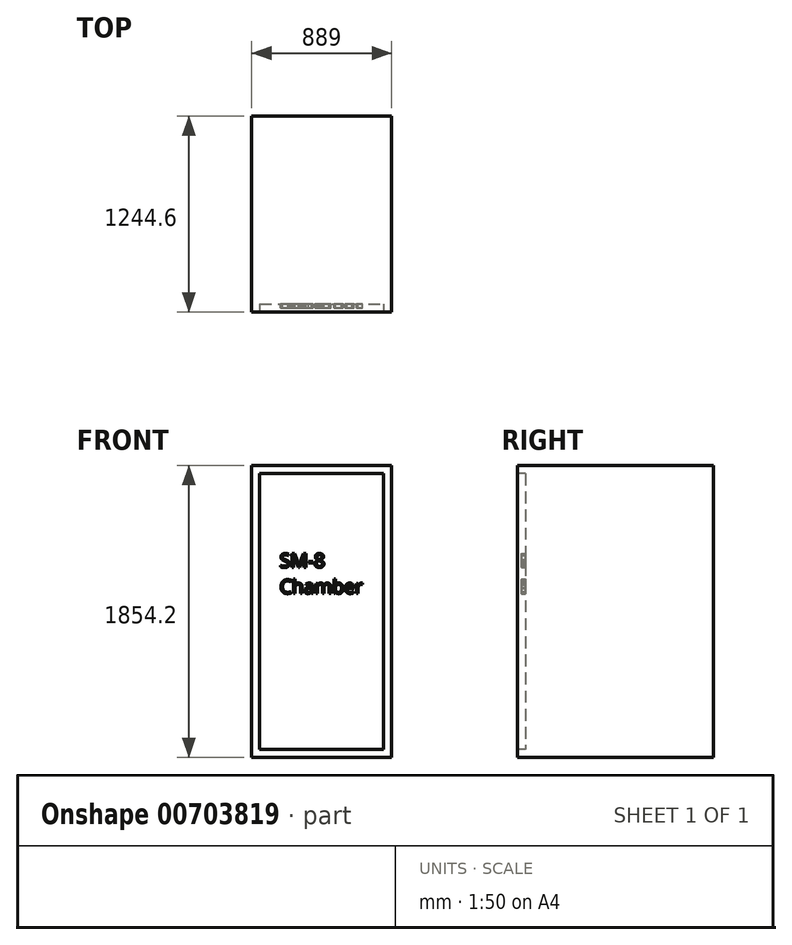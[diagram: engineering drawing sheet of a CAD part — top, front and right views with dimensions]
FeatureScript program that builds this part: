
annotation { "Feature Type Name" : "Feature", "Feature Type Description" : "" }
export const myFeature = defineFeature(function(context is Context, id is Id, definition is map)
    precondition{}
    {
        {
            var Q0;
            Q0=qCreatedBy(makeId("Top.planeOp"),FACE);
            var sketch = newSketch(context, id + "F0", { "sketchPlane" : qUnion([Q0])});
            skLineSegment(sketch, "E0.bottom", {"start": v(444.5, -622.3) * mm, "end": v(-444.5, -622.3) * mm});
            skLineSegment(sketch, "E0.top", {"start": v(444.5, 622.3) * mm, "end": v(-444.5, 622.3) * mm});
            skLineSegment(sketch, "E0.left", {"start": v(444.5, -622.3) * mm, "end": v(444.5, 622.3) * mm});
            skLineSegment(sketch, "E0.right", {"start": v(-444.5, -622.3) * mm, "end": v(-444.5, 622.3) * mm});
            skPoint(sketch, "E0.middle", {"position": v(0, 0) * mm});
            skSolve(sketch);
        }
        {
            var Q0;
            Q0 = qSketchRegion(id + "F0", true);
            extrude(context, id + "F1", {"entities" : qUnion([Q0]), "depth" : 1854.2 * mm, "offsetDistance" : 25.4 * mm});
        }
        {
            var Q0;
            Q0=makeQuery(id+"F1.opExtrude","SWEPT_FACE",FACE,{"disambiguationData":[OSD([sQuery(id+"F0.wireOp",EDGE,"E0.bottom")])]});
            var sketch = newSketch(context, id + "F2", { "sketchPlane" : qUnion([Q0])});
            skLineSegment(sketch, "E1.bottom", {"start": v(-393.7, 1803.4) * mm, "end": v(393.7, 1803.4) * mm});
            skLineSegment(sketch, "E1.top", {"start": v(-393.7, 50.8) * mm, "end": v(393.7, 50.8) * mm});
            skLineSegment(sketch, "E1.left", {"start": v(-393.7, 1803.4) * mm, "end": v(-393.7, 50.8) * mm});
            skLineSegment(sketch, "E1.right", {"start": v(393.7, 1803.4) * mm, "end": v(393.7, 50.8) * mm});
            skSolve(sketch);
        }
        {
            var Q0;
            Q0 = qSketchRegion(id + "F2", true);
            extrude(context, id + "F3", {"entities" : qUnion([Q0]), "operationType" : NewBodyOperationType.REMOVE, "oppositeDirection" : true, "depth" : 50.8 * mm, "offsetDistance" : 25.4 * mm});
        }
        {
            var Q0;
            Q0=makeQuery(id+"F3.boolean.opBoolean","COPY",FACE,{"derivedFrom":makeQuery(id+"F3.opExtrude","CAP_FACE",FACE,{"disambiguationData":[OSD([sQuery(id+"F2.wireOp",EDGE,"E1.bottom"),sQuery(id+"F2.wireOp",EDGE,"E1.top"),sQuery(id+"F2.wireOp",EDGE,"E1.left"),sQuery(id+"F2.wireOp",EDGE,"E1.right")])],"isStart":false})});
            var sketch = newSketch(context, id + "F4", { "sketchPlane" : qUnion([Q0])});
            skText(sketch, "E2", { "text": "SM-8\nChamber\n", "fontName": "OpenSans-Regular.ttf"});
            const initialGuessF4  = {"E2": [-0.2667, 1.2074, 1, 0, 0.088]};
            skSetInitialGuess(sketch, initialGuessF4);
            skSolve(sketch);
        }
        {
            var Q0;
            Q0 = qSketchRegion(id + "F4", true);
            extrude(context, id + "F5", {"entities" : qUnion([Q0]), "operationType" : NewBodyOperationType.ADD, "depth" : 25.4 * mm, "offsetDistance" : 25.4 * mm});
        }
    });
